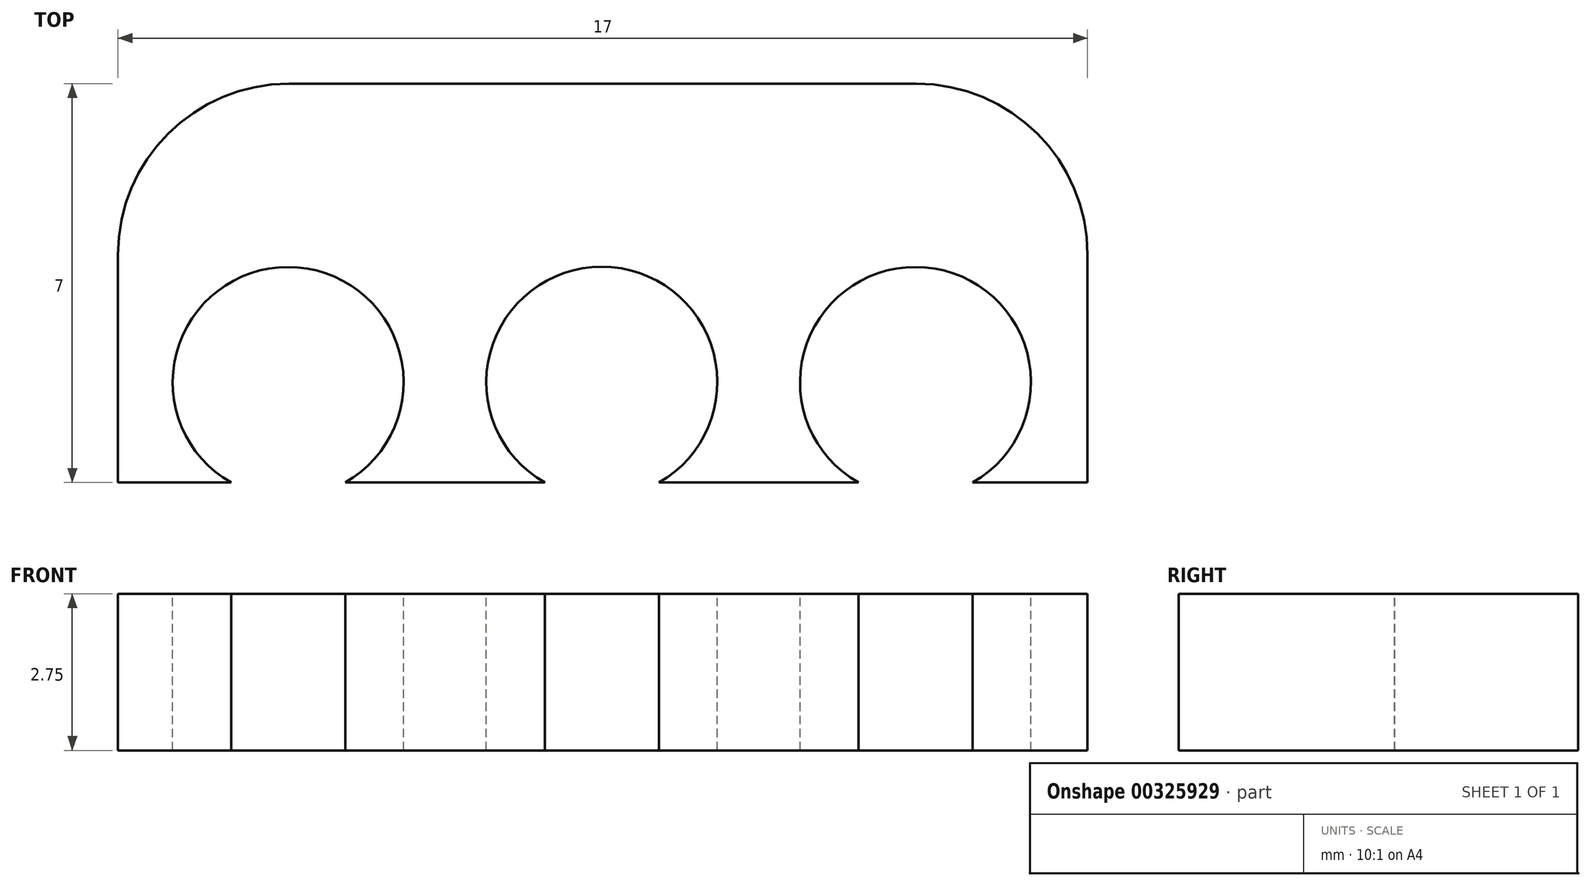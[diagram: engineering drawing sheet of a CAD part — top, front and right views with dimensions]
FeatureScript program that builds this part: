
annotation { "Feature Type Name" : "Feature", "Feature Type Description" : "" }
export const myFeature = defineFeature(function(context is Context, id is Id, definition is map)
    precondition{}
    {
        {
            var Q0;
            Q0=qCreatedBy(makeId("Top.planeOp"),FACE);
            var sketch = newSketch(context, id + "F0", { "sketchPlane" : qUnion([Q0])});
            skLineSegment(sketch, "E0.bottom", {"start": v(0, 0) * mm, "end": v(-17, 0) * mm});
            skLineSegment(sketch, "E0.top", {"start": v(0, 7) * mm, "end": v(-17, 7) * mm});
            skLineSegment(sketch, "E0.left", {"start": v(0, 0) * mm, "end": v(0, 7) * mm});
            skLineSegment(sketch, "E0.right", {"start": v(-17, 0) * mm, "end": v(-17, 7) * mm});
            skSolve(sketch);
        }
        {
            var Q0;
            Q0 = qSketchRegion(id + "F0", true);
            extrude(context, id + "F1", {"entities" : qUnion([Q0]), "depth" : 2.75 * mm});
        }
        {
            var Q0;
            Q0=makeQuery(id+"F1.opExtrude","CAP_FACE",FACE,{"disambiguationData":[OSD([sQuery(id+"F0.wireOp",EDGE,"E0.bottom"),sQuery(id+"F0.wireOp",EDGE,"E0.top"),sQuery(id+"F0.wireOp",EDGE,"E0.left"),sQuery(id+"F0.wireOp",EDGE,"E0.right")])],"isStart":false});
            var sketch = newSketch(context, id + "F2", { "sketchPlane" : qUnion([Q0])});
            skArc(sketch, "E1", {"start": v(-13.02, 0) * mm, "mid": v(-14.02, 3.78) * mm, "end": v(-15.02, 0) * mm});
            skArc(sketch, "E2", {"start": v(-7.52, 0) * mm, "mid": v(-8.52, 3.79) * mm, "end": v(-9.52, 0) * mm});
            skArc(sketch, "E3", {"start": v(-2.02, 0) * mm, "mid": v(-3.02, 3.78) * mm, "end": v(-4.02, 0) * mm});
            skSolve(sketch);
        }
        {
            var Q0;
            Q0 = qSketchRegion(id + "F2", true);
            var Q1;
            {var subQ0=sQuery(id+"F2.wireOp",EDGE,"E2");Q1=makeQuery(id+"F2.imprint","IMPRINT",FACE,{"disambiguationData":[TD([[makeQuery(id+"F2.imprint","IMPRINT",EDGE,{"derivedFrom":subQ0}),1.0]])]});}
            var Q2;
            {var subQ0=sQuery(id+"F2.wireOp",EDGE,"E3");Q2=makeQuery(id+"F2.imprint","IMPRINT",FACE,{"disambiguationData":[TD([[makeQuery(id+"F2.imprint","IMPRINT",EDGE,{"derivedFrom":subQ0}),1.0]])]});}
            var Q3;
            {var subQ0=sQuery(id+"F2.wireOp",EDGE,"E1");Q3=makeQuery(id+"F2.imprint","IMPRINT",FACE,{"disambiguationData":[TD([[makeQuery(id+"F2.imprint","IMPRINT",EDGE,{"derivedFrom":subQ0}),1.0]])]});}
            extrude(context, id + "F3", {"entities" : qUnion([Q0, Q1, Q2, Q3]), "operationType" : NewBodyOperationType.REMOVE, "oppositeDirection" : true, "depth" : 25 * mm});
        }
        {
            var Q0;
            Q0=makeQuery(id+"F1.opExtrude","SWEPT_EDGE",EDGE,{"disambiguationData":[OSD([sQuery(id+"F0.wireOp",EDGE,"E0.top"),sQuery(id+"F0.wireOp",EDGE,"E0.right")])]});
            var Q1;
            Q1=makeQuery(id+"F1.opExtrude","SWEPT_EDGE",EDGE,{"disambiguationData":[OSD([sQuery(id+"F0.wireOp",EDGE,"E0.top"),sQuery(id+"F0.wireOp",EDGE,"E0.left")])]});
            fillet(context, id + "F4", {"entities" : qUnion([Q0, Q1]), "radius" : 3 * mm, "tangentPropagation" : true, "allowEdgeOverflow" : false});
        }
    });
